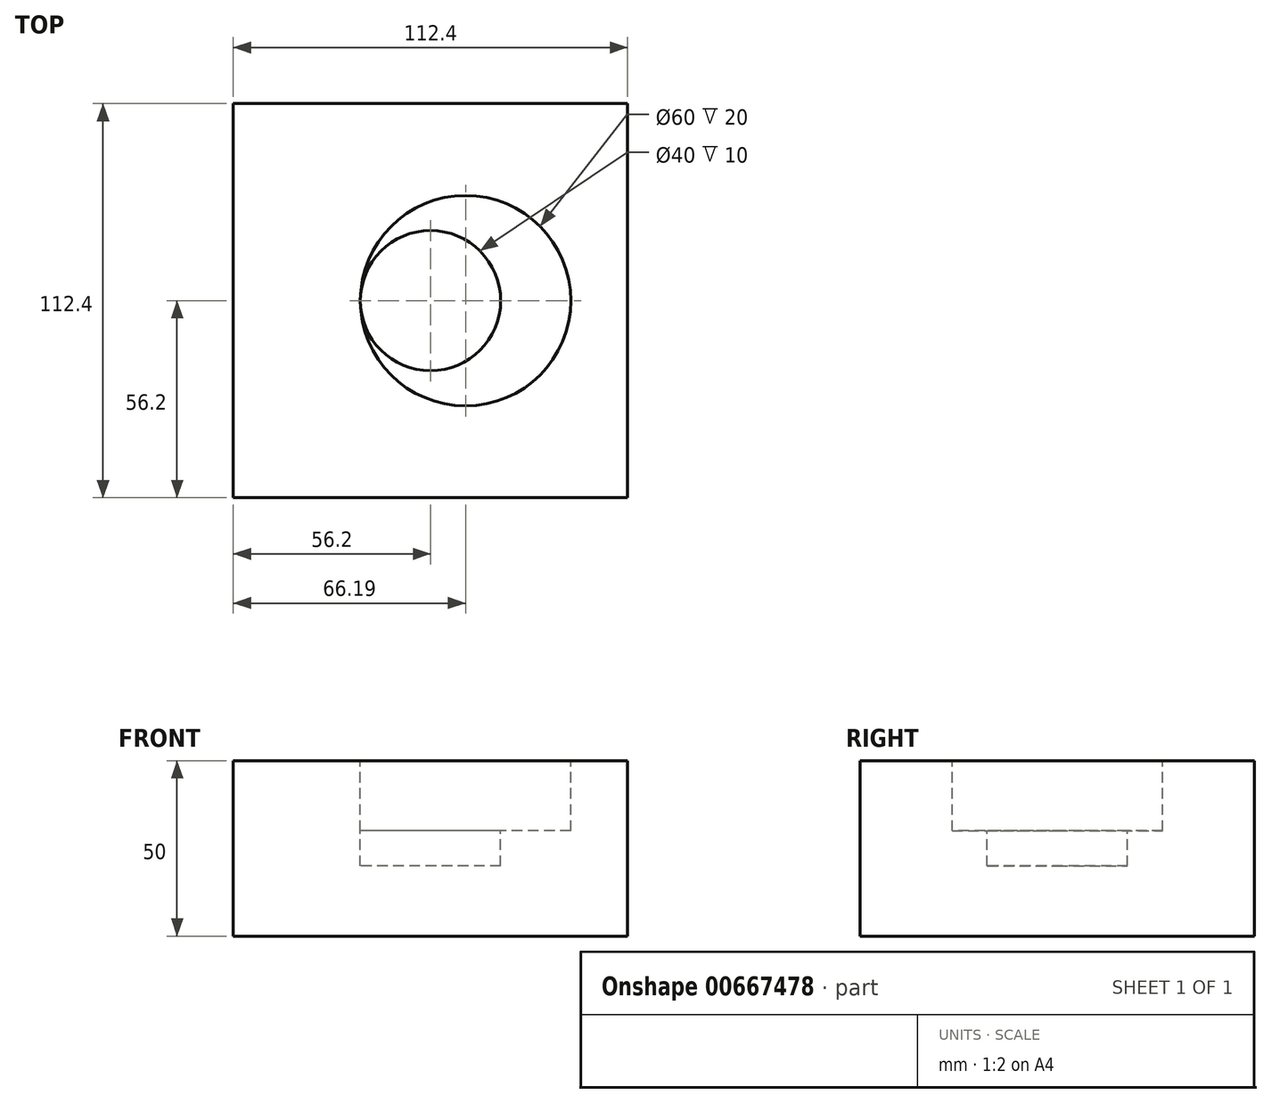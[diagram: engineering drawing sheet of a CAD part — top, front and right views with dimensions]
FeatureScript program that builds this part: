
annotation { "Feature Type Name" : "Feature", "Feature Type Description" : "" }
export const myFeature = defineFeature(function(context is Context, id is Id, definition is map)
    precondition{}
    {
        {
            var Q0;
            Q0=qCreatedBy(makeId("Top.planeOp"),FACE);
            var sketch = newSketch(context, id + "F0", { "sketchPlane" : qUnion([Q0])});
            skLineSegment(sketch, "E0.bottom", {"start": v(56.2, 56.2) * mm, "end": v(-56.2, 56.2) * mm});
            skLineSegment(sketch, "E0.top", {"start": v(56.2, -56.2) * mm, "end": v(-56.2, -56.2) * mm});
            skLineSegment(sketch, "E0.left", {"start": v(56.2, 56.2) * mm, "end": v(56.2, -56.2) * mm});
            skLineSegment(sketch, "E0.right", {"start": v(-56.2, 56.2) * mm, "end": v(-56.2, -56.2) * mm});
            skPoint(sketch, "E0.middle", {"position": v(0, 0) * mm});
            skSolve(sketch);
        }
        {
            var Q0;
            Q0=makeQuery(id+"F0.imprint","IMPRINT",FACE,{"disambiguationData":[TD([[makeQuery(id+"F0.imprint","IMPRINT",EDGE,{"derivedFrom":sQuery(id+"F0.wireOp",EDGE,"E0.bottom")}),1.0]])]});
            extrude(context, id + "F1", {"entities" : qUnion([Q0]), "depth" : 50 * mm, "offsetDistance" : 25 * mm});
        }
        {
            var Q0;
            Q0=makeQuery(id+"F1.opExtrude","CAP_FACE",FACE,{"disambiguationData":[OSD([sQuery(id+"F0.wireOp",EDGE,"E0.bottom"),sQuery(id+"F0.wireOp",EDGE,"E0.top"),sQuery(id+"F0.wireOp",EDGE,"E0.left"),sQuery(id+"F0.wireOp",EDGE,"E0.right")])],"isStart":false});
            var sketch = newSketch(context, id + "F2", { "sketchPlane" : qUnion([Q0])});
            skCircle(sketch, "E1", {"center": v(0, 0) * mm, "radius": 20 * mm});
            skCircle(sketch, "E2", {"center": v(9.99, 0) * mm, "radius": 30 * mm});
            skSolve(sketch);
        }
        {
            var Q0;
            Q0=makeQuery(id+"F2.imprint","IMPRINT",FACE,{"disambiguationData":[TD([[makeQuery(id+"F2.imprint","IMPRINT",EDGE,{"derivedFrom":sQuery(id+"F2.wireOp",EDGE,"E1")}),1.0]])]});
            extrude(context, id + "F3", {"entities" : qUnion([Q0]), "operationType" : NewBodyOperationType.REMOVE, "oppositeDirection" : true, "depth" : 30 * mm, "offsetDistance" : 25 * mm});
        }
        {
            var Q0;
            Q0=makeQuery(id+"F2.imprint","IMPRINT",FACE,{"disambiguationData":[TD([[makeQuery(id+"F2.imprint","IMPRINT",EDGE,{"derivedFrom":sQuery(id+"F2.wireOp",EDGE,"E1")}),-1.0]])]});
            extrude(context, id + "F4", {"entities" : qUnion([Q0]), "operationType" : NewBodyOperationType.REMOVE, "oppositeDirection" : true, "depth" : 20 * mm, "offsetDistance" : 25 * mm});
        }
    });
